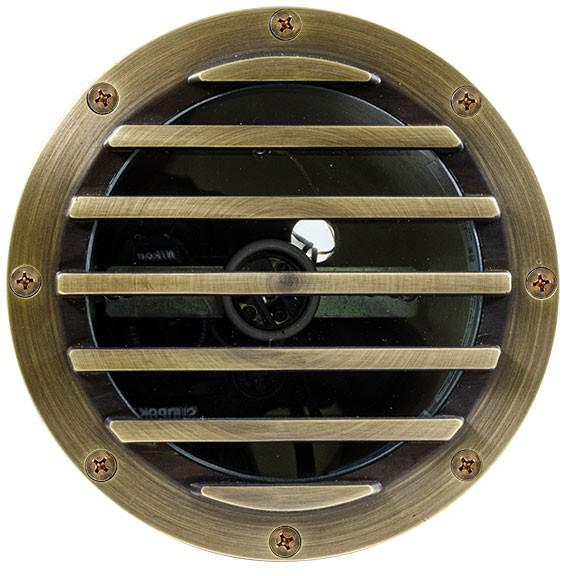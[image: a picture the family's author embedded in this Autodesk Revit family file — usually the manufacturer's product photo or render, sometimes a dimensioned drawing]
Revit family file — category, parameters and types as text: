
# Revit family: Alcon-9069-Revit-Family
name_source: partatom
category: Luminarias
units: mm (PartAtom-declared; Revit-internal decimal feet)

## family parameters
Anfitrión = Cara
Compartido = No
Corte con vacíos al cargar = No
Cota de conector redondo = Usar diámetro
Mantener orientación de anotación = No
Origen de luz = Sí
Punto de cálculo de habitación = No
Tipo de pieza = Normal

## types (1)
- Alcon-9069-Revit-Family
    Cambio de temperatura de color de luz atenuada = <Ninguno>
    Elevación por defecto = 4' - 0"
    Fabricante = Alcon Lighting
    Filtro de color = 16777215
    GLASS LENS = Analytical Panels
    HOUSING = <Por categoría>
    LENS GLASS = Glass
    Link to IES File = https://www.alconlighting.com
    Longitud de símbolo de origen de luz = 10' - 0"
    Modelo = Alcon Lighting 9069
    Product Data URL = https://www.alconlighting.com
    Product Page = https://www.alconlighting.com
    TAP LENS = <Por categoría>
    TOP FINISH = <Por categoría>
    URL = https://www.alconlighting.com
    Ángulo de campo de foco = 90.00°
    Ángulo de enfoque = 30.00°
    Ángulo de inclinación = 60.00°

## geometry (parser evidence)
native form markers: Sweep x3
no freeform markers — native parametric forms only
